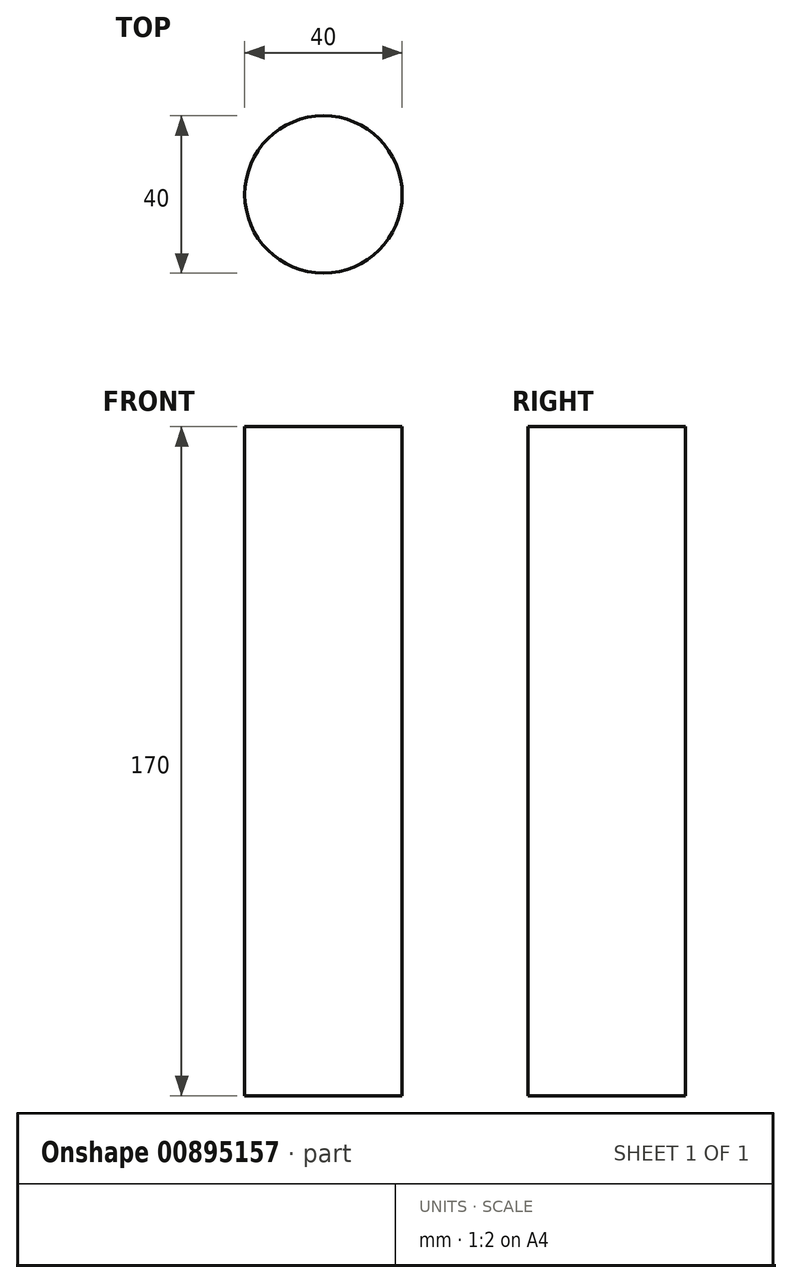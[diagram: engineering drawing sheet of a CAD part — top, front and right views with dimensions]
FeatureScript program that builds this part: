
annotation { "Feature Type Name" : "Feature", "Feature Type Description" : "" }
export const myFeature = defineFeature(function(context is Context, id is Id, definition is map)
    precondition{}
    {
        {
            var Q0;
            Q0=qCreatedBy(makeId("Front.planeOp"),FACE);
            var sketch = newSketch(context, id + "F0", { "sketchPlane" : qUnion([Q0])});
            skLineSegment(sketch, "E0.bottom", {"start": v(-20, 0) * mm, "end": v(0, 0) * mm});
            skLineSegment(sketch, "E0.top", {"start": v(-20, 170) * mm, "end": v(0, 170) * mm});
            skLineSegment(sketch, "E0.left", {"start": v(-20, 0) * mm, "end": v(-20, 170) * mm});
            skLineSegment(sketch, "E0.right", {"start": v(0, 0) * mm, "end": v(0, 170) * mm});
            skSolve(sketch);
        }
        {
            var Q0;
            Q0=makeQuery(id+"F0.imprint","IMPRINT",FACE,{"disambiguationData":[TD([[makeQuery(id+"F0.imprint","IMPRINT",EDGE,{"derivedFrom":sQuery(id+"F0.wireOp",EDGE,"E0.bottom")}),1.0]])]});
            var Q1;
            Q1=sQuery(id+"F0.wireOp",EDGE,"E0.right");
            revolve(context, id + "F1", {"surfaceOperationType" : NewSurfaceOperationType.NEW, "entities" : qUnion([Q0]), "axis" : qUnion([Q1]), "revolveType" : RevolveType.FULL});
        }
    });
